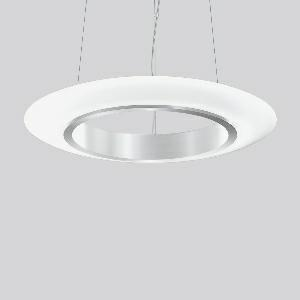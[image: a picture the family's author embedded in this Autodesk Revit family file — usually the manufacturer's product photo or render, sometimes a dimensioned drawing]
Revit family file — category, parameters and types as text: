
# Revit family: ring_of_fire_p_311570_004_76_9af4
name_source: partatom
category: Lighting Fixtures
units: mm (PartAtom-declared; Revit-internal decimal feet)

## family parameters
Cut with Voids When Loaded = No
Host = Face
Light Source = No
Part Type = Normal
Room Calculation Point = No
Round Connector Dimension = Use Diameter
Shared = No

## types (1)
- RING OF FIRE P (1 x LED Modul 830, 4050 lm, 3000)
    Apparent Load = 37 VA
    CIE Flux Codes = 43 73 90 55 100
    Color Rendering = 80
    Color Temperature = 3000
    Default Elevation = 1800 mm
    Description = Series: RING OF FIRE
A uniquely shaped pendant luminaire with elliptical glass. Supporting ring made of anodised aluminium. Canopy aluminium anodised. Opal glass: mouth-blown, satin finish. Suitable for pendant. 3-point steel cable suspension, steplessly adjustable. Special lengths available on request. For pendant lengths of up to 2 m, power is supplied through a suspension cable. For pendant lengths of 2 m and more, power must be supplied through a separate cable. Converter integrated in the canopy. TouchDim sensor capable. Light and/or presence sensors can be integrated. 
Colour: anodised aluminium
Diameter: 690 mm
Height: 81 mm
Suspension length: 500-1200 mm
Lamp: LED
Socket: without socket
Colour temperature: 3000K
Colour rendering index (CRI): 80
System power: 37 W
Rated luminous flux: 4050 lm
Luminous efficiency: 109 lm/W
Control gear: Converter, dimmable, DALI
Protection class: I
Type of protection: IP 20
    Height = 81 mm
    Lamp = 1 x LED Modul 830
    Lamp Light Flux = 4050 lm
    Lamp count = 1
    Length = 690 mm
    Lifetime = 50000 h
    Luminous efficacy = 109 lm/W
    Manufacturer = RZB
    ModVariant = No
    Model = 311570.004.76
    Mounting Place = Ceiling
    Mounting Type = Pendant
    Number of Poles = 1
    OnlyDefault = Yes
    Power Factor = 1
    Product Name = RING OF FIRE P
    Product group = Pendant luminaires
    ProductGroupID = 902
    Protection Class = Protection class I
    Protection Degree = IP 20
    RLX_Detail_Level = 1
    RLX_Emergency_Light_Flux = 0 lm
    RLX_Emergency_Type = 0
    RLX_Emergency_Type_DB = No
    RlxData = <blob elided: 30561 chars, md5=60ee1a36>
    Socket = socket
    Standby Power = 0 W
    System Light Flux = 4050 lm
    System Power = 37 W
    Type Comments = Product without accessories
    Type Image = 311570.004.jpg
    URL = http://relux.com
    VarID = ---
    Voltage = 230 V
    Voltage Range = 220-240 V
    Weight = 0.00 kg
    Width = 0 mm  [stored 0 ft]

note: [stored X ft] marks values corroborated as IEEE doubles in the binary element streams (Revit-internal decimal feet)

## geometry (parser evidence)
native form markers: Blend x4, Sweep x13
no freeform markers — native parametric forms only
